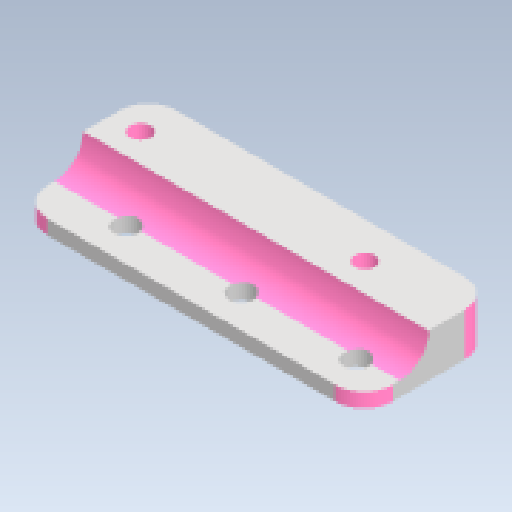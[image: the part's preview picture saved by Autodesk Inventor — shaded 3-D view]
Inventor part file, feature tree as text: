
AUTODESK INVENTOR PART (.ipt)
format: ipt  version: 2023 (Build 270158000, 158)  size: 136,192 bytes
history: native  units: in
note: dims shown in document units (in); Inventor stores cm internally (conversion verified against a paired STEP export)
features: other x3, sketch x2, fillet x1
ambient origin geometry x8: Origin, YZ Plane, XZ Plane, XY Plane, X Axis, Y Axis, Z Axis, Center Point
bodies: Solid1 (feature_tree)
feature tree (6):
  other  "DriveMotorMount5.ipt"
  fillet  "Fillet1"  Radius=0.3937in
  other  "Solid1::DriveMotorMount5.ipt"
  other  "TaggingFeature1"
  sketch  "Sketch1"  dims[d1=0.25in]
  sketch  "Sketch2"
